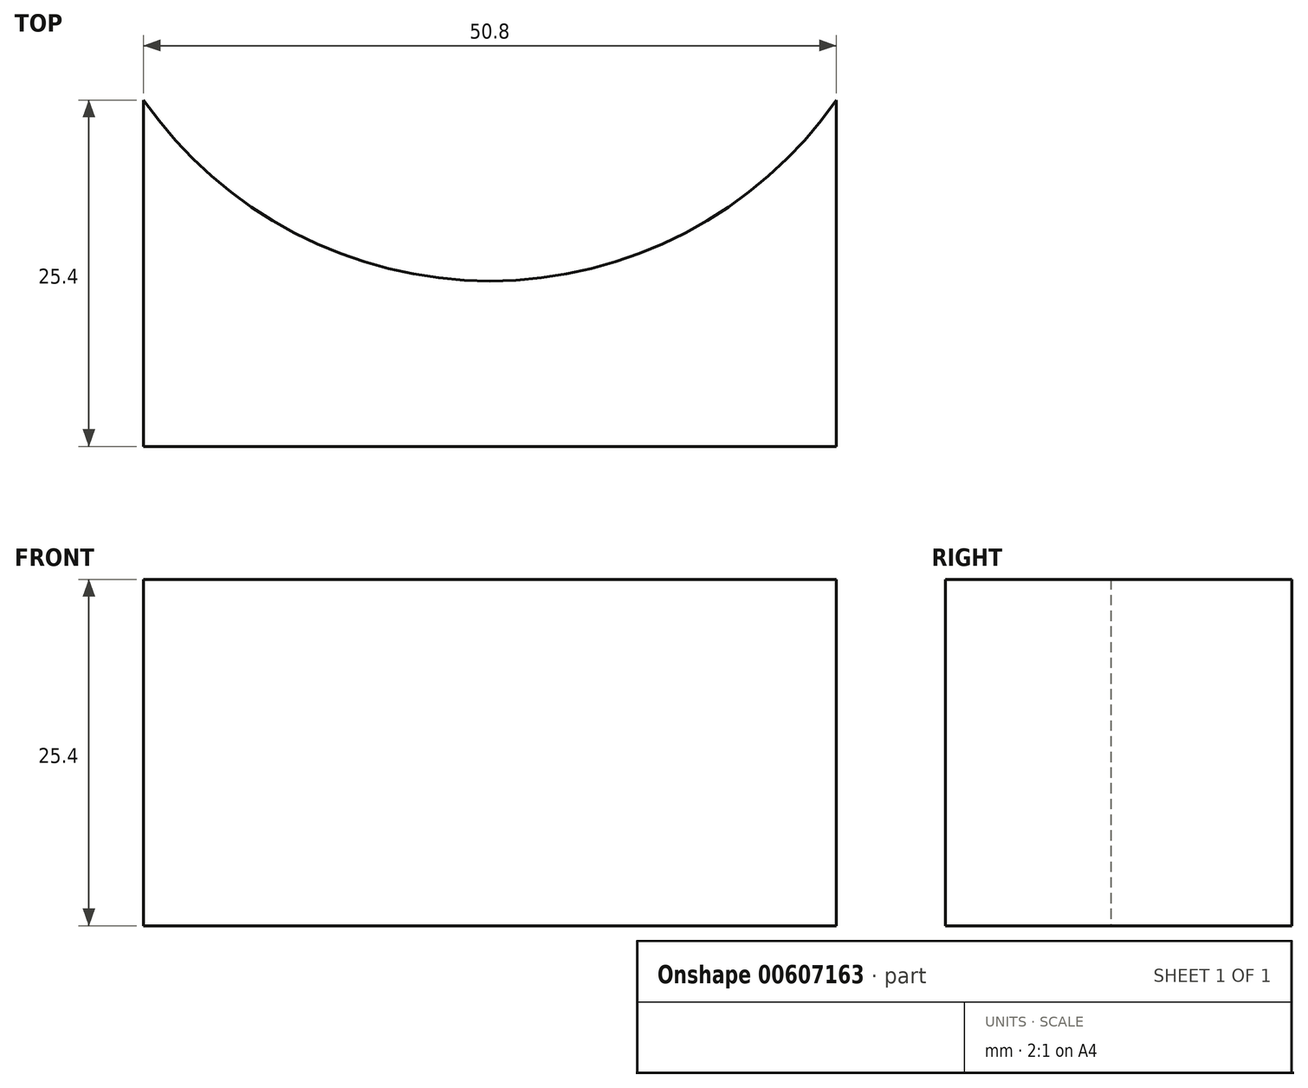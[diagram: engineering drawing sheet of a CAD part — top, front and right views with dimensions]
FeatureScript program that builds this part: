
annotation { "Feature Type Name" : "Feature", "Feature Type Description" : "" }
export const myFeature = defineFeature(function(context is Context, id is Id, definition is map)
    precondition{}
    {
        {
            var Q0;
            Q0=qCreatedBy(makeId("Top.planeOp"),FACE);
            var sketch = newSketch(context, id + "F0", { "sketchPlane" : qUnion([Q0])});
            skLineSegment(sketch, "E0.top", {"start": v(-24.25, -25.4) * mm, "end": v(26.55, -25.4) * mm});
            skLineSegment(sketch, "E0.left", {"start": v(-24.25, 0) * mm, "end": v(-24.25, -25.4) * mm});
            skLineSegment(sketch, "E0.right", {"start": v(26.55, 0) * mm, "end": v(26.55, -25.4) * mm});
            skArc(sketch, "E1", {"start": v(-24.25, 0) * mm, "mid": v(1.15, -13.27) * mm, "end": v(26.55, 0) * mm});
            skSolve(sketch);
        }
        {
            var Q0;
            Q0=makeQuery(id+"F0.imprint","IMPRINT",FACE,{"disambiguationData":[TD([[makeQuery(id+"F0.imprint","IMPRINT",EDGE,{"derivedFrom":sQuery(id+"F0.wireOp",EDGE,"E0.top")}),1.0]])]});
            extrude(context, id + "F1", {"entities" : qUnion([Q0]), "depth" : 25.4 * mm, "offsetDistance" : 25.4 * mm});
        }
    });
